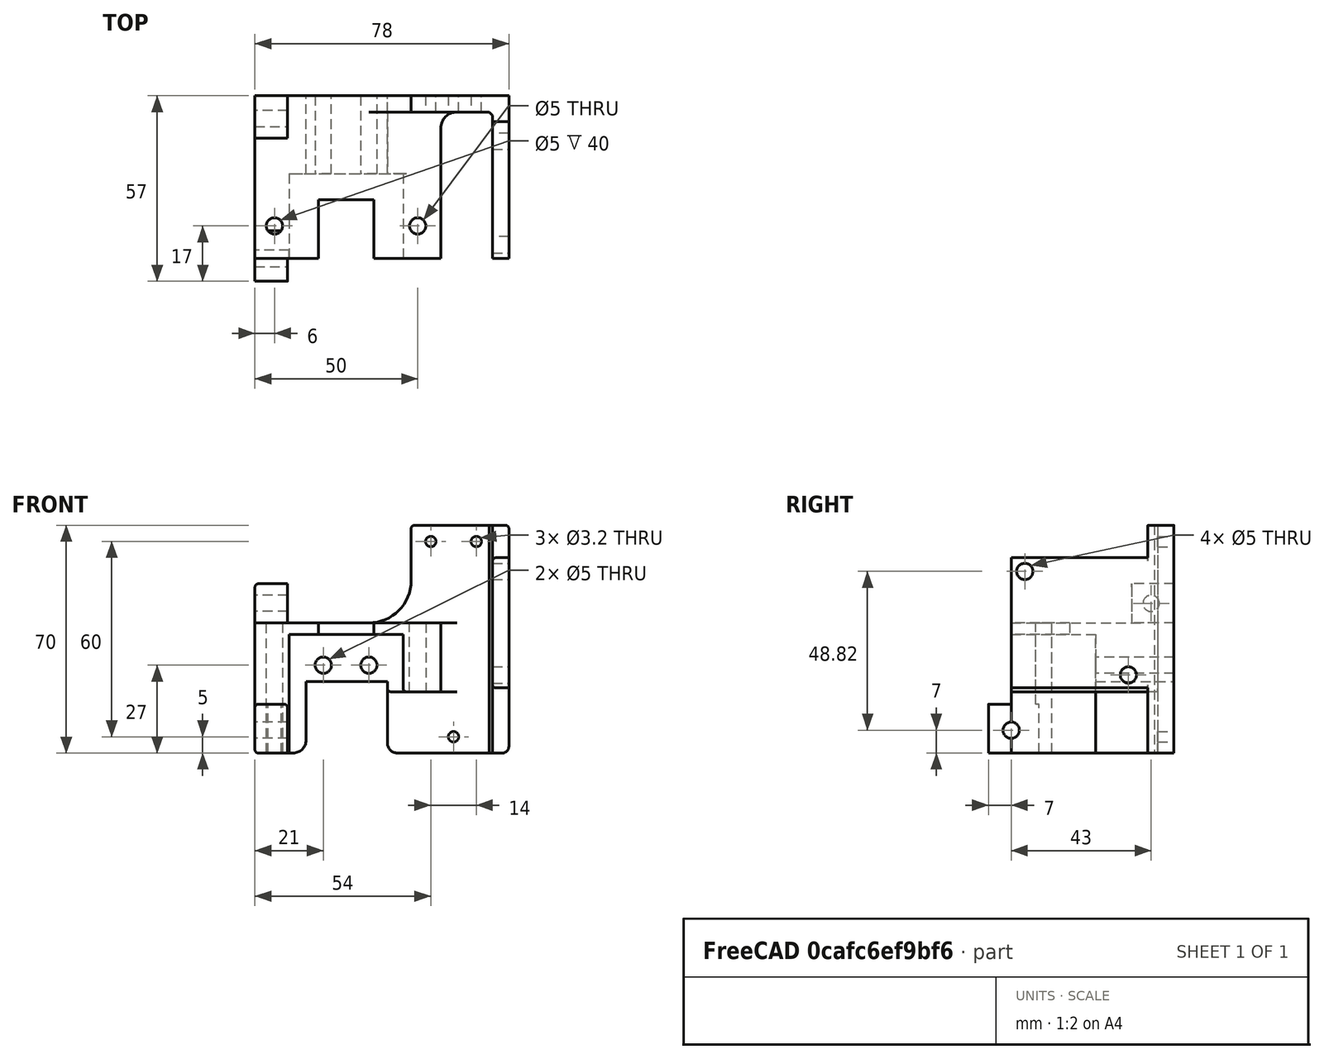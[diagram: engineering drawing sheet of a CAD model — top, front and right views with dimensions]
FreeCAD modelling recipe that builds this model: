
FCSTD DOCUMENT  (FreeCAD 0.19R)
Label: head
License: All rights reserved
LicenseURL: http://en.wikipedia.org/wiki/All_rights_reserved
objects: Sketcher::SketchObject×14, PartDesign::Fillet×13, PartDesign::Pocket×12, PartDesign::Pad×2, PartDesign::Chamfer×1, PartDesign::Body×1, Mesh::Feature×1
note: 71 computed .brp shape members not serialized (recipe doc carries the construction recipe); baked Part::Feature solids carry a one-line shape summary decoded from their .brp

FEATURE [Sketcher::SketchObject] Sketch
  FullyConstrained = true
  MapMode = 5
  Support = -> [XY_Plane]
  sketch-geometry (5):
    g0: LineSegment StartX=0 StartY=0 StartZ=0 EndX=50 EndY=0 EndZ=0
    g1: LineSegment StartX=-28 StartY=0 StartZ=0 EndX=0 EndY=0 EndZ=0
    g2: LineSegment StartX=-28 StartY=0 StartZ=0 EndX=-28 EndY=-50 EndZ=0
    g3: LineSegment StartX=-28 StartY=-50 StartZ=0 EndX=50 EndY=-50 EndZ=0
    g4: LineSegment StartX=50 StartY=-50 StartZ=0 EndX=50 EndY=0 EndZ=0
  constraints (14):
    c: Coincident(g-1,g0)
    c: PointOnObject(g0,g-1)
    c: PointOnObject(g1,g-1)
    c: Coincident(g1,g0)
    c: Coincident(g1,g2)
    c: Vertical(g2)
    c: Coincident(g2,g3)
    c: Horizontal(g3)
    c: Coincident(g3,g4)
    c: Coincident(g4,g0)
    c: Vertical(g4)
    c: Distance(g4) = 50
    c: DistanceX(g0) = 50
    c: DistanceX(g1) = -28
FEATURE [PartDesign::Pad] Pad
  Direction = (1,1,1)
  Length = 70
  Length2 = 100
  Profile = -> Sketch
  Type = 0
FEATURE [Sketcher::SketchObject] Sketch001
  FullyConstrained = false
  MapMode = 5
  Placement = pos=(0,0,70) rot=(0,0,1;0rad)
  Support = -> [Pad]
  sketch-geometry (4):
    g0: LineSegment StartX=29.0717 StartY=-5 StartZ=0 EndX=45 EndY=-5 EndZ=0
    g1: LineSegment StartX=45 StartY=-5 StartZ=0 EndX=45 EndY=-51.78 EndZ=0
    g2: LineSegment StartX=45 StartY=-51.78 StartZ=0 EndX=29.0717 EndY=-51.78 EndZ=0
    g3: LineSegment StartX=29.0717 StartY=-51.78 StartZ=0 EndX=29.0717 EndY=-5 EndZ=0
  constraints (11):
    c: Coincident(g0,g1)
    c: Coincident(g1,g2)
    c: Coincident(g2,g3)
    c: Coincident(g3,g0)
    c: Horizontal(g0)
    c: Horizontal(g2)
    c: Vertical(g1)
    c: Vertical(g3)
    c: DistanceX(g0) = 45
    c: DistanceY(g1) = -51.78
    c: DistanceY(g0) = -5
FEATURE [PartDesign::Pocket] Pocket  label="BOBnotch"
  BaseFeature = -> Pad
  Length = 5
  Length2 = 100
  Profile = -> Sketch001
  Type = 1
FEATURE [Sketcher::SketchObject] Sketch002
  FullyConstrained = false
  MapMode = 5
  Placement = pos=(0,0,70) rot=(0,0,1;0rad)
  Support = -> [Pocket]
  sketch-geometry (6):
    g0: LineSegment StartX=30 StartY=-5 StartZ=0 EndX=30 EndY=-65.096 EndZ=0
    g1: LineSegment StartX=30 StartY=-65.096 StartZ=0 EndX=-40.7834 EndY=-65.096 EndZ=0
    g2: LineSegment StartX=-40.7834 StartY=-65.096 StartZ=0 EndX=-40.7834 EndY=12.9948 EndZ=0
    g3: LineSegment StartX=-40.7834 StartY=12.9948 StartZ=0 EndX=20 EndY=12.9948 EndZ=0
    g4: LineSegment StartX=20 StartY=12.9948 StartZ=0 EndX=20 EndY=-5 EndZ=0
    g5: LineSegment StartX=20 StartY=-5 StartZ=0 EndX=30 EndY=-5 EndZ=0
  constraints (15):
    c: Coincident(g0,g1)
    c: Coincident(g1,g2)
    c: Horizontal(g1)
    c: Vertical(g0)
    c: Vertical(g2)
    c: DistanceX(g0) = 30
    c: DistanceY(g0) = -5
    c: Coincident(g2,g3)
    c: Horizontal(g3)
    c: Coincident(g3,g4)
    c: Coincident(g4,g5)
    c: Coincident(g5,g0)
    c: Horizontal(g5)
    c: Vertical(g4)
    c: DistanceX(g3) = 20
FEATURE [PartDesign::Pocket] Pocket001  label="stepperplatform"
  BaseFeature = -> Pocket
  Length = 30
  Length2 = 100
  Profile = -> Sketch002
  Type = 0
FEATURE [Sketcher::SketchObject] Sketch003
  FullyConstrained = true
  MapMode = 5
  Placement = pos=(0,0,40) rot=(0,0,1;0rad)
  Support = -> [Pocket001]
  sketch-geometry (2):
    g0: Circle CenterX=-22 CenterY=-40 CenterZ=0 NormalX=0 NormalY=0 NormalZ=1 AngleXU=0 Radius=2.5
    g1: Circle CenterX=22 CenterY=-40 CenterZ=0 NormalX=0 NormalY=0 NormalZ=1 AngleXU=0 Radius=2.5
  constraints (5):
    c: Radius(g1) = 2.5
    c: Equal(g1,g0)
    c: Symmetric(g1,g0,g-2)
    c: Distance(g1,g0) = 44
    c: DistanceY(g0) = -40
FEATURE [PartDesign::Pocket] Pocket002  label="steppermountholes"
  BaseFeature = -> Pocket001
  Length = 5
  Length2 = 100
  Profile = -> Sketch003
  Type = 1
FEATURE [Sketcher::SketchObject] Sketch004
  FullyConstrained = false
  MapMode = 5
  Placement = pos=(0,0,40) rot=(0,0,1;0rad)
  Support = -> [Pocket002]
  sketch-geometry (4):
    g0: LineSegment StartX=-8.5 StartY=-32 StartZ=0 EndX=8.5 EndY=-32 EndZ=0
    g1: LineSegment StartX=8.5 StartY=-32 StartZ=0 EndX=8.5 EndY=-55.3144 EndZ=0
    g2: LineSegment StartX=8.5 StartY=-55.3144 StartZ=0 EndX=-8.5 EndY=-55.3144 EndZ=0
    g3: LineSegment StartX=-8.5 StartY=-55.3144 StartZ=0 EndX=-8.5 EndY=-32 EndZ=0
  constraints (10):
    c: Coincident(g0,g1)
    c: Coincident(g1,g2)
    c: Coincident(g2,g3)
    c: Coincident(g3,g0)
    c: Horizontal(g2)
    c: Vertical(g1)
    c: Vertical(g3)
    c: Symmetric(g0,g0,g-2)
    c: DistanceY(g0) = -32
    c: Distance(g0) = 17
FEATURE [PartDesign::Pocket] Pocket003  label="hotendnotch001"
  BaseFeature = -> Pocket002
  Length = 5
  Length2 = 100
  Profile = -> Sketch004
  Type = 1
FEATURE [Sketcher::SketchObject] Sketch005
  FullyConstrained = false
  MapMode = 5
  Placement = pos=(0,-50,0) rot=(1,0,0;1.5708rad)
  Support = -> [Pocket003]
  sketch-geometry (4):
    g0: LineSegment StartX=-17.5 StartY=36.5 StartZ=0 EndX=17.5 EndY=36.5 EndZ=0
    g1: LineSegment StartX=17.5 StartY=36.5 StartZ=0 EndX=17.5 EndY=-21.4748 EndZ=0
    g2: LineSegment StartX=17.5 StartY=-21.4748 StartZ=0 EndX=-17.5 EndY=-21.4748 EndZ=0
    g3: LineSegment StartX=-17.5 StartY=-21.4748 StartZ=0 EndX=-17.5 EndY=36.5 EndZ=0
  constraints (10):
    c: Coincident(g0,g1)
    c: Coincident(g1,g2)
    c: Coincident(g2,g3)
    c: Coincident(g3,g0)
    c: Horizontal(g2)
    c: Vertical(g1)
    c: Vertical(g3)
    c: Symmetric(g0,g0,g-2)
    c: Distance(g0) = 35
    c: DistanceY(g0) = 36.5
FEATURE [PartDesign::Pocket] Pocket004  label="hotendnotch"
  BaseFeature = -> Pocket003
  Length = 26
  Length2 = 100
  Profile = -> Sketch005
  Type = 0
FEATURE [Sketcher::SketchObject] Sketch006
  FullyConstrained = false
  MapMode = 5
  Placement = pos=(0,-24,5.9e-15) rot=(1,0,0;1.5708rad)
  Support = -> [Pocket004]
  sketch-geometry (4):
    g0: LineSegment StartX=-12.2861 StartY=22 StartZ=0 EndX=12.7139 EndY=22 EndZ=0
    g1: LineSegment StartX=12.7139 StartY=22 StartZ=0 EndX=12.7139 EndY=-8.26916 EndZ=0
    g2: LineSegment StartX=12.7139 StartY=-8.26916 StartZ=0 EndX=-12.2861 EndY=-8.26916 EndZ=0
    g3: LineSegment StartX=-12.2861 StartY=-8.26916 StartZ=0 EndX=-12.2861 EndY=22 EndZ=0
  constraints (10):
    c: Coincident(g0,g1)
    c: Coincident(g1,g2)
    c: Coincident(g2,g3)
    c: Coincident(g3,g0)
    c: Horizontal(g0)
    c: Horizontal(g2)
    c: Vertical(g1)
    c: Vertical(g3)
    c: Distance(g0) = 25
    c: DistanceY(g0) = 22
FEATURE [PartDesign::Pocket] Pocket005  label="fanclearance"
  BaseFeature = -> Pocket004
  Length = 5
  Length2 = 100
  Profile = -> Sketch006
  Type = 1
FEATURE [Sketcher::SketchObject] Sketch007
  FullyConstrained = false
  MapMode = 5
  Placement = pos=(0,-50,0) rot=(1,0,0;1.5708rad)
  Support = -> [Pocket005]
  sketch-geometry (4):
    g0: LineSegment StartX=7.61208 StartY=18.8386 StartZ=0 EndX=33.8542 EndY=18.8386 EndZ=0
    g1: LineSegment StartX=33.8542 StartY=18.8386 StartZ=0 EndX=33.8542 EndY=-10.9025 EndZ=0
    g2: LineSegment StartX=33.8542 StartY=-10.9025 StartZ=0 EndX=7.61208 EndY=-10.9025 EndZ=0
    g3: LineSegment StartX=7.61208 StartY=-10.9025 StartZ=0 EndX=7.61208 EndY=18.8386 EndZ=0
  constraints (8):
    c: Coincident(g0,g1)
    c: Coincident(g1,g2)
    c: Coincident(g2,g3)
    c: Coincident(g3,g0)
    c: Horizontal(g0)
    c: Horizontal(g2)
    c: Vertical(g1)
    c: Vertical(g3)
FEATURE [PartDesign::Pocket] Pocket006  label="bottomconnectorclearance"
  BaseFeature = -> Pocket005
  Length = 45
  Length2 = 100
  Profile = -> Sketch007
  Type = 0
FEATURE [Sketcher::SketchObject] Sketch008
  FullyConstrained = false
  MapMode = 5
  Placement = pos=(0,-50,0) rot=(1,0,0;1.5708rad)
  Support = -> [Pocket006]
  sketch-geometry (8):
    g0: LineSegment StartX=35.0962 StartY=76.3926 StartZ=0 EndX=50.7218 EndY=76.3926 EndZ=0
    g1: LineSegment StartX=50.7218 StartY=76.3926 StartZ=0 EndX=50.7218 EndY=60 EndZ=0
    g2: LineSegment StartX=50.7218 StartY=60 StartZ=0 EndX=35.0962 EndY=60 EndZ=0
    g3: LineSegment StartX=35.0962 StartY=60 StartZ=0 EndX=35.0962 EndY=76.3926 EndZ=0
    g4: LineSegment StartX=34.0545 StartY=20 StartZ=0 EndX=58.6648 EndY=20 EndZ=0
    g5: LineSegment StartX=58.6648 StartY=20 StartZ=0 EndX=58.6648 EndY=-12.6735 EndZ=0
    g6: LineSegment StartX=58.6648 StartY=-12.6735 StartZ=0 EndX=34.0545 EndY=-12.6735 EndZ=0
    g7: LineSegment StartX=34.0545 StartY=-12.6735 StartZ=0 EndX=34.0545 EndY=20 EndZ=0
  constraints (18):
    c: Coincident(g0,g1)
    c: Coincident(g1,g2)
    c: Coincident(g2,g3)
    c: Coincident(g3,g0)
    c: Horizontal(g0)
    c: Horizontal(g2)
    c: Vertical(g1)
    c: Vertical(g3)
    c: Coincident(g4,g5)
    c: Coincident(g5,g6)
    c: Coincident(g6,g7)
    c: Coincident(g7,g4)
    c: Horizontal(g4)
    c: Horizontal(g6)
    c: Vertical(g5)
    c: Vertical(g7)
    c: DistanceY(g2) = 60
    c: DistanceY(g4) = 20
FEATURE [PartDesign::Pocket] Pocket007  label="BOBnotches"
  BaseFeature = -> Pocket006
  Length = 42
  Length2 = 100
  Profile = -> Sketch008
  Type = 0
FEATURE [Sketcher::SketchObject] Sketch009
  FullyConstrained = true
  MapMode = 5
  Placement = pos=(50,0,0) rot=(0.57735,0.57735,0.57735;2.0944rad)
  Support = -> [Pocket007]
  sketch-geometry (3):
    g0: Circle CenterX=-45.8198 CenterY=55.8198 CenterZ=0 NormalX=0 NormalY=0 NormalZ=1 AngleXU=0 Radius=2.5
    g1: Circle CenterX=-14 CenterY=24 CenterZ=0 NormalX=0 NormalY=0 NormalZ=1 AngleXU=0 Radius=2.5
    g2: LineSegment StartX=-45.8198 StartY=55.8198 StartZ=0 EndX=-14 EndY=24 EndZ=0
  constraints (8):
    c: Diameter(g1) = 5
    c: Equal(g1,g0)
    c: Distance(g0,g1) = 45
    c: Coincident(g2,g0)
    c: Coincident(g2,g1)
    c: Angle(g2) = -0.785398
    c: DistanceX(g1) = -14
    c: DistanceY(g1) = 24
FEATURE [PartDesign::Pocket] Pocket008  label="stepperholes"
  BaseFeature = -> Pocket007
  Length = 13
  Length2 = 100
  Profile = -> Sketch009
  Type = 0
FEATURE [Sketcher::SketchObject] Sketch010
  FullyConstrained = true
  MapMode = 5
  Placement = pos=(0,0,0) rot=(0,0.707107,0.707107;3.14159rad)
  Support = -> [Pocket008]
  sketch-geometry (3):
    g0: Circle CenterX=-33 CenterY=5 CenterZ=0 NormalX=0 NormalY=0 NormalZ=1 AngleXU=0 Radius=1.6
    g1: Circle CenterX=-40 CenterY=65 CenterZ=0 NormalX=0 NormalY=0 NormalZ=1 AngleXU=0 Radius=1.6
    g2: Circle CenterX=-26 CenterY=65 CenterZ=0 NormalX=0 NormalY=0 NormalZ=1 AngleXU=0 Radius=1.6
  constraints (9):
    c: Diameter(g0) = 3.2
    c: Equal(g0,g2)
    c: Equal(g0,g1)
    c: DistanceX(g0) = -33
    c: Distance(g1,g2) = 14
    c: DistanceX(g2) = -26
    c: DistanceY(g0) = 5
    c: DistanceY(g2) = 65
    c: DistanceY(g1) = 65
FEATURE [PartDesign::Pocket] Pocket009  label="mountholes"
  BaseFeature = -> Pocket008
  Length = 5
  Length2 = 100
  Profile = -> Sketch010
  Type = 0
FEATURE [Sketcher::SketchObject] Sketch012
  FullyConstrained = false
  MapMode = 5
  Placement = pos=(-28,0,0) rot=(0.57735,-0.57735,-0.57735;2.0944rad)
  Support = -> [Pocket009]
  sketch-geometry (8):
    g0: LineSegment StartX=0 StartY=52 StartZ=0 EndX=13 EndY=52 EndZ=0
    g1: LineSegment StartX=13 StartY=52 StartZ=0 EndX=13 EndY=38 EndZ=0
    g2: LineSegment StartX=13 StartY=38 StartZ=0 EndX=0 EndY=38 EndZ=0
    g3: LineSegment StartX=0 StartY=38 StartZ=0 EndX=0 EndY=52 EndZ=0
    g4: LineSegment StartX=41.4627 StartY=15 StartZ=0 EndX=57 EndY=15 EndZ=0
    g5: LineSegment StartX=57 StartY=15 StartZ=0 EndX=57 EndY=0 EndZ=0
    g6: LineSegment StartX=57 StartY=0 StartZ=0 EndX=41.4627 EndY=0 EndZ=0
    g7: LineSegment StartX=41.4627 StartY=0 StartZ=0 EndX=41.4627 EndY=15 EndZ=0
  constraints (23):
    c: Coincident(g0,g1)
    c: Coincident(g1,g2)
    c: Coincident(g2,g3)
    c: Coincident(g3,g0)
    c: Horizontal(g0)
    c: Horizontal(g2)
    c: Vertical(g1)
    c: Vertical(g3)
    c: PointOnObject(g2,g-2)
    c: DistanceY(g0) = 52
    c: DistanceX(g0) = 13
    c: Distance(g1) = 14
    c: Coincident(g4,g5)
    c: Coincident(g5,g6)
    c: Coincident(g6,g7)
    c: Coincident(g7,g4)
    c: Horizontal(g4)
    c: Horizontal(g6)
    c: Vertical(g5)
    c: Vertical(g7)
    c: PointOnObject(g5,g-1)
    c: DistanceX(g5) = 57
    c: DistanceY(g4) = 15
FEATURE [PartDesign::Pad] Pad001
  BaseFeature = -> Pocket009
  Direction = (1,1,1)
  Length = 10
  Length2 = 100
  Profile = -> Sketch012
  Reversed = true
  Type = 0
FEATURE [Sketcher::SketchObject] Sketch011
  FullyConstrained = true
  MapMode = 5
  Placement = pos=(-28,0,0) rot=(0.57735,-0.57735,-0.57735;2.0944rad)
  Support = -> [Pad001]
  sketch-geometry (2):
    g0: Circle CenterX=50 CenterY=7 CenterZ=0 NormalX=0 NormalY=0 NormalZ=1 AngleXU=0 Radius=2.5
    g1: Circle CenterX=7 CenterY=46 CenterZ=0 NormalX=0 NormalY=0 NormalZ=1 AngleXU=0 Radius=2.5
  constraints (6):
    c: Diameter(g0) = 5
    c: DistanceY(g0) = 7
    c: DistanceX(g0) = 50
    c: Diameter(g1) = 5
    c: DistanceY(g1) = 46
    c: DistanceX(g1) = 7
FEATURE [PartDesign::Pocket] Pocket010
  BaseFeature = -> Pad001
  Length = 11
  Length2 = 100
  Profile = -> Sketch011
  Type = 0
FEATURE [Sketcher::SketchObject] Sketch013
  ExternalGeometry = -> [Pocket010]
  FullyConstrained = true
  MapMode = 5
  Placement = pos=(0,-24,5.9e-15) rot=(1,0,0;1.5708rad)
  Support = -> [Pocket010]
  sketch-geometry (2):
    g0: Circle CenterX=-7 CenterY=27 CenterZ=0 NormalX=0 NormalY=0 NormalZ=1 AngleXU=0 Radius=2.5
    g1: Circle CenterX=7 CenterY=27 CenterZ=0 NormalX=0 NormalY=0 NormalZ=1 AngleXU=0 Radius=2.5
  constraints (5):
    c: Symmetric(g1,g0,g-2)
    c: Distance(g1,g0) = 14
    c: DistanceY(g1,g-3) = 9.5
    c: Diameter(g1) = 5
    c: Equal(g1,g0)
FEATURE [PartDesign::Pocket] Pocket011
  BaseFeature = -> Pocket010
  Length = 5
  Length2 = 100
  Profile = -> Sketch013
  Type = 1
FEATURE [PartDesign::Chamfer] Chamfer
  Angle = 45
  Base = -> Pocket011 [Edge77]
  BaseFeature = -> Pocket011
  ChamferType = 0
  FlipDirection = false
  Size = 1
  Size2 = 1
  SupportTransform = false
FEATURE [PartDesign::Fillet] Fillet
  Base = -> Chamfer [Edge95]
  BaseFeature = -> Chamfer
  Radius = 13
  SupportTransform = false
FEATURE [PartDesign::Fillet] Fillet001
  Base = -> Fillet [Edge83]
  BaseFeature = -> Fillet
  Radius = 5
  SupportTransform = false
FEATURE [PartDesign::Fillet] Fillet002
  Base = -> Fillet001 [Edge117]
  BaseFeature = -> Fillet001
  Radius = 2
  SupportTransform = false
FEATURE [PartDesign::Fillet] Fillet003
  Base = -> Fillet002 [Edge138]
  BaseFeature = -> Fillet002
  Radius = 1
  SupportTransform = false
FEATURE [PartDesign::Fillet] Fillet004
  Base = -> Fillet003 [Edge186]
  BaseFeature = -> Fillet003
  Radius = 1
  SupportTransform = false
FEATURE [PartDesign::Fillet] Fillet005
  Base = -> Fillet004 [Edge180,Edge182]
  BaseFeature = -> Fillet004
  Radius = 1
  SupportTransform = false
FEATURE [PartDesign::Fillet] Fillet006
  Base = -> Fillet005 [Edge97]
  BaseFeature = -> Fillet005
  Radius = 4
  SupportTransform = false
FEATURE [PartDesign::Fillet] Fillet007
  Base = -> Fillet006 [Edge102]
  BaseFeature = -> Fillet006
  Radius = 1
  SupportTransform = false
FEATURE [PartDesign::Fillet] Fillet008
  Base = -> Fillet007 [Edge24]
  BaseFeature = -> Fillet007
  Radius = 1
  SupportTransform = false
FEATURE [PartDesign::Fillet] Fillet009
  Base = -> Fillet008 [Edge200,Edge198]
  BaseFeature = -> Fillet008
  Radius = 1
  SupportTransform = false
FEATURE [PartDesign::Fillet] Fillet010
  Base = -> Fillet009 [Edge37]
  BaseFeature = -> Fillet009
  Radius = 3
  SupportTransform = false
FEATURE [PartDesign::Fillet] Fillet011
  Base = -> Fillet010 [Edge76]
  BaseFeature = -> Fillet010
  Radius = 1
  SupportTransform = false
FEATURE [PartDesign::Fillet] Fillet012
  Base = -> Fillet011 [Edge21]
  BaseFeature = -> Fillet011
  Radius = 1
  SupportTransform = false
FEATURE [PartDesign::Body] Body
  Group = -> [Sketch,Pad,Sketch001,Pocket,Sketch002,Pocket001,Sketch003,Pocket002,Sketch004,Pocket003,Sketch005,Pocket004,Sketch006,Pocket005,Sketch007,Pocket006,Sketch008,Pocket007,Sketch009,Pocket008,Sketch010,Pocket009,Sketch011,Sketch012,Pad001,Pocket010,Sketch013,Pocket011,Chamfer,Fillet,Fillet001,Fillet002,Fillet003,Fillet004,Fillet005,Fillet006,Fillet007,Fillet008,Fillet009,Fillet010,Fillet011,Fillet012]
  Origin = -> Origin
  Tip = -> Fillet012
FEATURE [Mesh::Feature] Mesh  label="Fillet012 (Meshed)"
